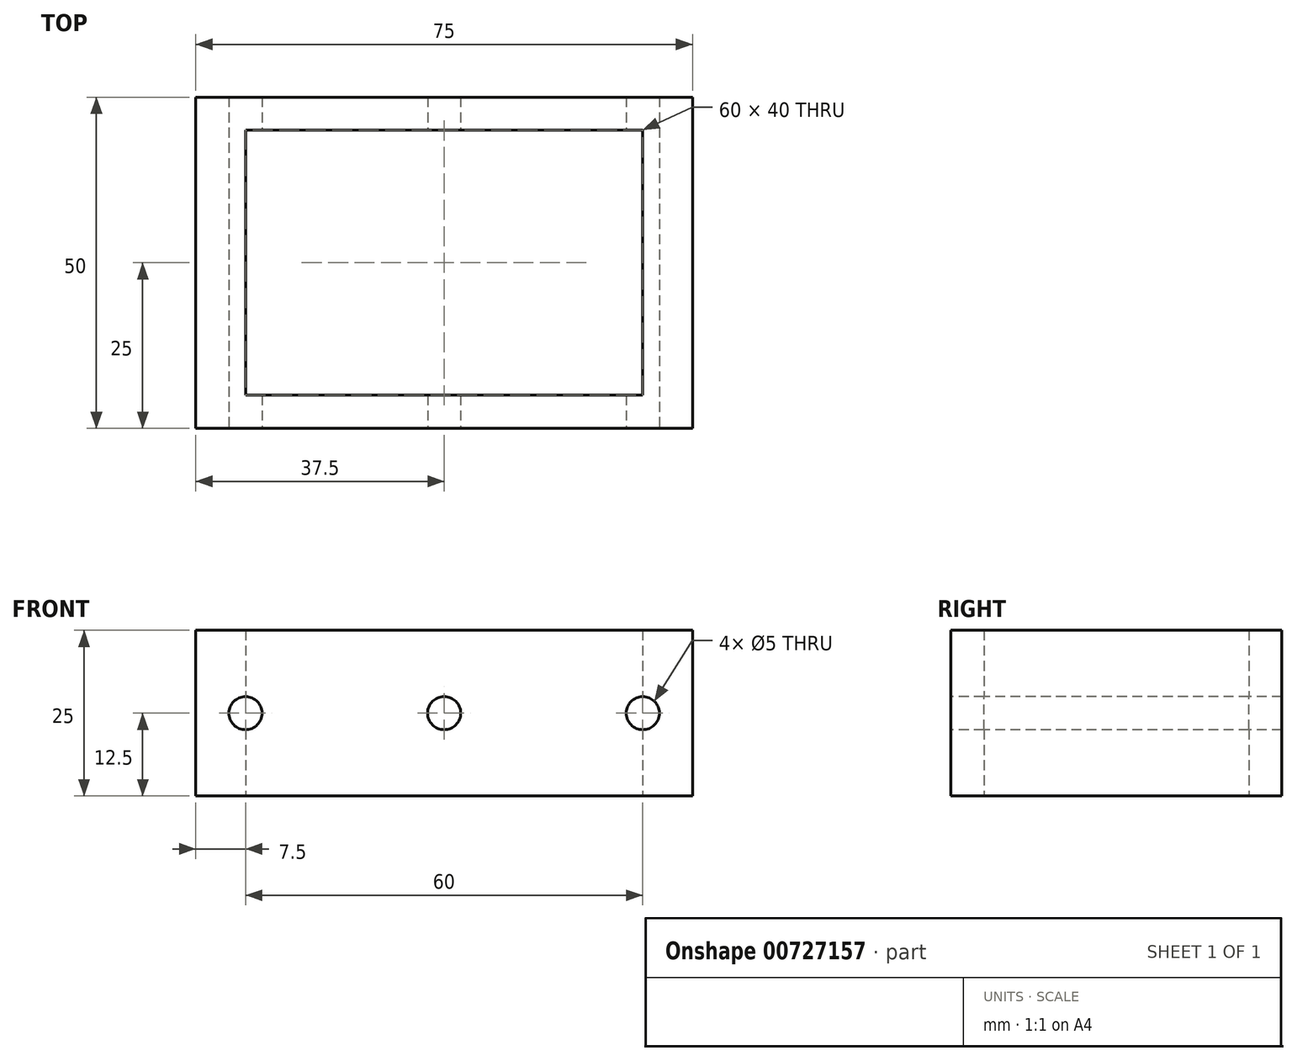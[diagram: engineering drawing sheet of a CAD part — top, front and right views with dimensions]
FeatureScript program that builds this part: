
annotation { "Feature Type Name" : "Feature", "Feature Type Description" : "" }
export const myFeature = defineFeature(function(context is Context, id is Id, definition is map)
    precondition{}
    {
        {
            var Q0;
            Q0=qCreatedBy(makeId("Top.planeOp"),FACE);
            var sketch = newSketch(context, id + "F0", { "sketchPlane" : qUnion([Q0])});
            skLineSegment(sketch, "E0.bottom", {"start": v(37.5, -25) * mm, "end": v(-37.5, -25) * mm});
            skLineSegment(sketch, "E0.top", {"start": v(37.5, 25) * mm, "end": v(-37.5, 25) * mm});
            skLineSegment(sketch, "E0.left", {"start": v(37.5, -25) * mm, "end": v(37.5, 25) * mm});
            skLineSegment(sketch, "E0.right", {"start": v(-37.5, -25) * mm, "end": v(-37.5, 25) * mm});
            skPoint(sketch, "E0.middle", {"position": v(0, 0) * mm});
            skLineSegment(sketch, "E1.bottom", {"start": v(30, -20) * mm, "end": v(-30, -20) * mm});
            skLineSegment(sketch, "E1.top", {"start": v(30, 20) * mm, "end": v(-30, 20) * mm});
            skLineSegment(sketch, "E1.left", {"start": v(30, -20) * mm, "end": v(30, 20) * mm});
            skLineSegment(sketch, "E1.right", {"start": v(-30, -20) * mm, "end": v(-30, 20) * mm});
            skSolve(sketch);
        }
        {
            var Q0;
            Q0 = qSketchRegion(id + "F0", true);
            extrude(context, id + "F1", {"entities" : qUnion([Q0]), "endBound" : BoundingType.SYMMETRIC, "depth" : 25 * mm, "offsetDistance" : 25.4 * mm});
        }
        {
            var Q0;
            Q0=qCreatedBy(makeId("Front.planeOp"),FACE);
            var sketch = newSketch(context, id + "F2", { "sketchPlane" : qUnion([Q0])});
            skCircle(sketch, "E2", {"center": v(-30, 0) * mm, "radius": 2.5 * mm});
            skCircle(sketch, "E3", {"center": v(30, 0) * mm, "radius": 2.5 * mm});
            skCircle(sketch, "E4", {"center": v(0, 0) * mm, "radius": 2.5 * mm});
            skSolve(sketch);
        }
        {
            var Q0;
            Q0 = qSketchRegion(id + "F2", true);
            extrude(context, id + "F3", {"entities" : qUnion([Q0]), "operationType" : NewBodyOperationType.REMOVE, "endBound" : BoundingType.THROUGH_ALL, "oppositeDirection" : true, "depth" : 25.4 * mm, "offsetDistance" : 25.4 * mm, "hasSecondDirection" : true, "secondDirectionBound" : SecondDirectionBoundingType.THROUGH_ALL, "secondDirectionOppositeDirection" : false, "secondDirectionDepth" : 25.4 * mm});
        }
    });
